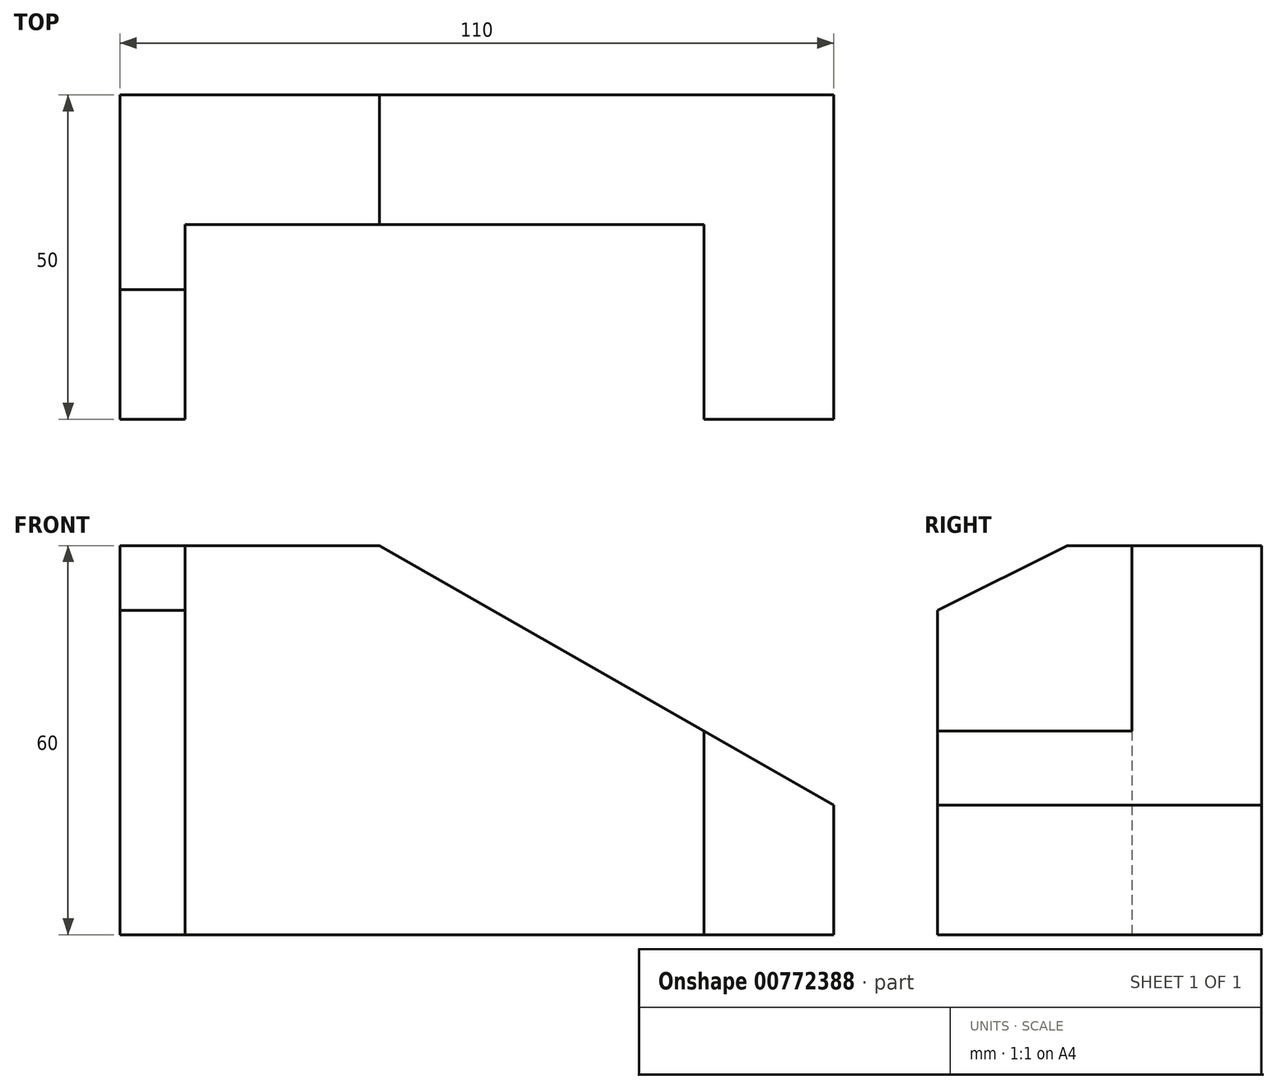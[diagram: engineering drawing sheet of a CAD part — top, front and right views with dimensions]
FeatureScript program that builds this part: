
annotation { "Feature Type Name" : "Feature", "Feature Type Description" : "" }
export const myFeature = defineFeature(function(context is Context, id is Id, definition is map)
    precondition{}
    {
        {
            var Q0;
            Q0=qCreatedBy(makeId("Top.planeOp"),FACE);
            var sketch = newSketch(context, id + "F0", { "sketchPlane" : qUnion([Q0])});
            skLineSegment(sketch, "E0", {"start": v(0, 0) * mm, "end": v(110, 0) * mm});
            skLineSegment(sketch, "E1", {"start": v(110, 0) * mm, "end": v(110, -50) * mm});
            skLineSegment(sketch, "E2", {"start": v(110, -50) * mm, "end": v(90, -50) * mm});
            skLineSegment(sketch, "E3", {"start": v(90, -50) * mm, "end": v(90, -20) * mm});
            skLineSegment(sketch, "E4", {"start": v(90, -20) * mm, "end": v(10, -20) * mm});
            skLineSegment(sketch, "E5", {"start": v(10, -20) * mm, "end": v(10, -50) * mm});
            skLineSegment(sketch, "E6", {"start": v(10, -50) * mm, "end": v(0, -50) * mm});
            skLineSegment(sketch, "E7", {"start": v(0, -50) * mm, "end": v(0, 0) * mm});
            skSolve(sketch);
        }
        {
            var Q0;
            Q0=makeQuery(id+"F0.imprint","IMPRINT",FACE,{"disambiguationData":[TD([[makeQuery(id+"F0.imprint","IMPRINT",EDGE,{"derivedFrom":sQuery(id+"F0.wireOp",EDGE,"E0")}),-1.0]])]});
            extrude(context, id + "F1", {"entities" : qUnion([Q0]), "depth" : 60 * mm, "offsetDistance" : 25 * mm});
        }
        {
            var Q0;
            Q0=makeQuery(id+"F1.opExtrude","CAP_EDGE",EDGE,{"disambiguationData":[OSD([sQuery(id+"F0.wireOp",EDGE,"E6")])],"isStart":false});
            chamfer(context, id + "F2", {"entities" : qUnion([Q0]), "chamferType" : ChamferType.TWO_OFFSETS, "width1" : 10 * mm, "oppositeDirection" : false, "width2" : 20 * mm, "tangentPropagation" : true});
        }
        {
            var Q0;
            Q0=makeQuery(id+"F1.opExtrude","CAP_EDGE",EDGE,{"disambiguationData":[OSD([sQuery(id+"F0.wireOp",EDGE,"E1")])],"isStart":false});
            chamfer(context, id + "F3", {"entities" : qUnion([Q0]), "chamferType" : ChamferType.TWO_OFFSETS, "width1" : (60 - 20) * mm, "oppositeDirection" : false, "width2" : 70 * mm, "tangentPropagation" : true});
        }
    });
